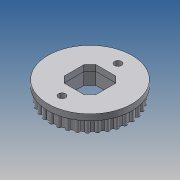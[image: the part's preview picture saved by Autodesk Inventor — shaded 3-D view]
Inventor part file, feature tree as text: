
AUTODESK INVENTOR PART (.ipt)
format: ipt  version: 2017 (Build 210142000, 142)  size: 238,080 bytes
history: native  units: mm
features: other x4, extrude x2, sketch x2, reference x2
ambient origin geometry x8: Origin, YZ Plane, XZ Plane, XY Plane, X Axis, Y Axis, Z Axis, Center Point
bodies: Body1 (feature_tree), Body2 (feature_tree)
feature tree (10):
  other  "Sólido1"
  extrude  "Extrusión1"  Depth=6.0mm TaperAngle=0.0deg
  extrude  "Extrusión3"  Depth=3.0mm
  sketch  "Boceto1"  dims[d0=38.31mm d1=6.0mm d2=0.0mm]
  reference  "Referencia1"
  sketch  "Boceto3"  dims[d4=3.0mm d16=2.0mm d17=340.0mm d19=360.0deg d22=3.0mm d23=0.0mm d24=43.31mm d25=3.534801mm d27=2.5mm]
  other  "Sólido3"
  reference  "Referencia6"
  other  "Conjunto polea motor 2.iam"
  other  "dado polea correa motor:1"
